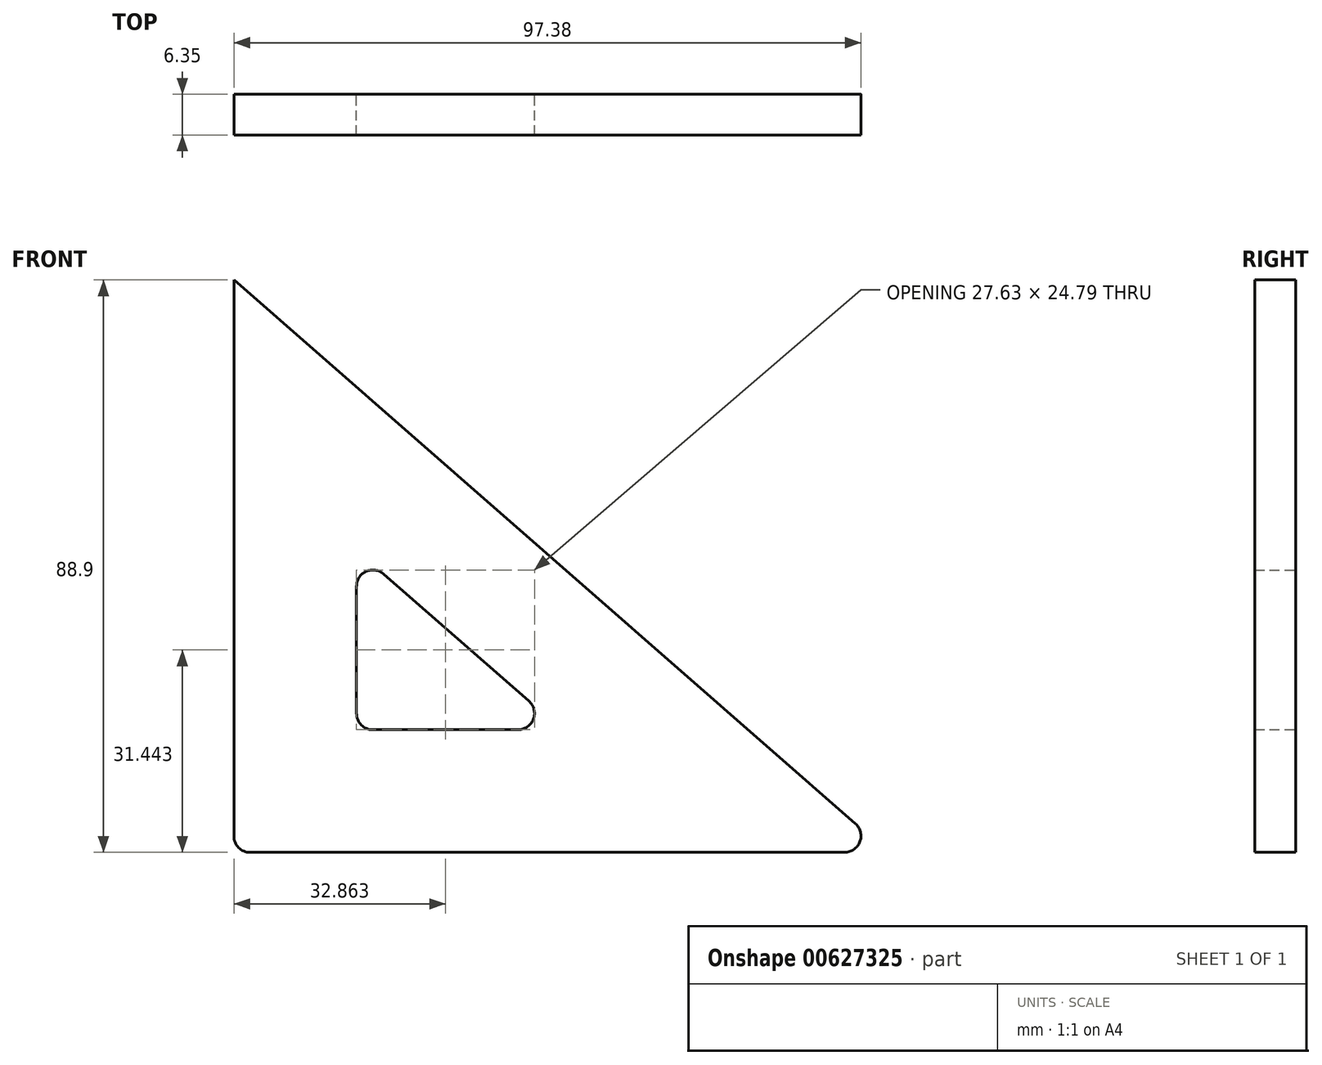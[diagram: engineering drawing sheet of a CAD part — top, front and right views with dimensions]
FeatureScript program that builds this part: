
annotation { "Feature Type Name" : "Feature", "Feature Type Description" : "" }
export const myFeature = defineFeature(function(context is Context, id is Id, definition is map)
    precondition{}
    {
        {
            var Q0;
            Q0=qCreatedBy(makeId("Front.planeOp"),FACE);
            var sketch = newSketch(context, id + "F0", { "sketchPlane" : qUnion([Q0])});
            skLineSegment(sketch, "E0", {"start": v(-6.76, 0) * mm, "end": v(-99.06, 0) * mm});
            skLineSegment(sketch, "E1", {"start": v(-101.6, 88.9) * mm, "end": v(-101.6, 2.54) * mm});
            skLineSegment(sketch, "E2", {"start": v(-101.6, 88.9) * mm, "end": v(-5.09, 4.45) * mm});
            skLineSegment(sketch, "E3.0", {"start": v(-78.34, 43.23) * mm, "end": v(-55.79, 23.5) * mm});
            skLineSegment(sketch, "E3.1", {"start": v(-82.55, 41.32) * mm, "end": v(-82.55, 21.59) * mm});
            skLineSegment(sketch, "E3.2", {"start": v(-57.46, 19.05) * mm, "end": v(-80.01, 19.05) * mm});
            skPoint(sketch, "E4.visualSharp", {"position": v(-82.55, 46.92) * mm});
            skArc(sketch, "E4.filletArc", {"start": v(-78.34, 43.23) * mm, "mid": v(-81.06, 43.63) * mm, "end": v(-82.55, 41.32) * mm});
            skPoint(sketch, "E5.visualSharp", {"position": v(-82.55, 19.05) * mm});
            skArc(sketch, "E5.filletArc", {"start": v(-82.55, 21.59) * mm, "mid": v(-81.8, 19.8) * mm, "end": v(-80.01, 19.05) * mm});
            skPoint(sketch, "E6.visualSharp", {"position": v(-50.7, 19.05) * mm});
            skArc(sketch, "E6.filletArc", {"start": v(-57.46, 19.05) * mm, "mid": v(-55.08, 20.7) * mm, "end": v(-55.79, 23.5) * mm});
            skPoint(sketch, "E7.visualSharp", {"position": v(-101.6, 0) * mm});
            skArc(sketch, "E7.filletArc", {"start": v(-101.6, 2.54) * mm, "mid": v(-100.86, 0.74) * mm, "end": v(-99.06, 0) * mm});
            skPoint(sketch, "E8.visualSharp", {"position": v(0, 0) * mm});
            skArc(sketch, "E8.filletArc", {"start": v(-6.76, 0) * mm, "mid": v(-4.38, 1.65) * mm, "end": v(-5.09, 4.45) * mm});
            skSolve(sketch);
        }
        {
            var Q0;
            Q0=makeQuery(id+"F0.imprint","IMPRINT",FACE,{"disambiguationData":[TD([[makeQuery(id+"F0.imprint","IMPRINT",EDGE,{"derivedFrom":sQuery(id+"F0.wireOp",EDGE,"E0")}),-1.0]])]});
            extrude(context, id + "F1", {"entities" : qUnion([Q0]), "depth" : 6.35 * mm, "offsetDistance" : 25.4 * mm});
        }
    });
